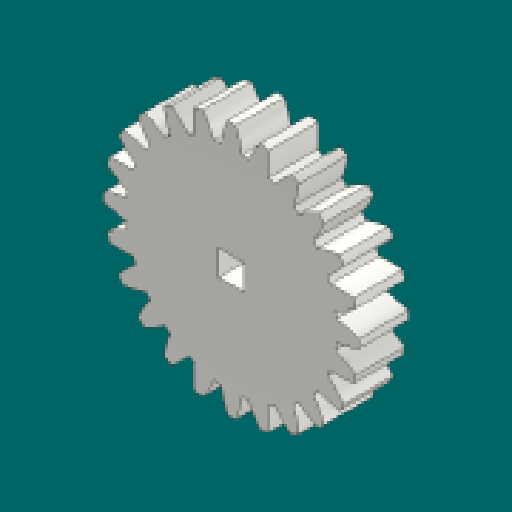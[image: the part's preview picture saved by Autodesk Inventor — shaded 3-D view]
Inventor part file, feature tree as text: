
AUTODESK INVENTOR PART (.ipt)
format: ipt  version: 2023.1 (Build 271208000, 208)  size: 255,488 bytes
history: native  units: mm (DEFAULTED — no unit token found)
features: plane x3, other x3, sketch x3, extrude x2
ambient origin geometry x8: Origin, YZ Plane, XZ Plane, XY Plane, X Axis, Y Axis, Z Axis, Center Point
bodies: Solid1 (feature_tree)
feature tree (11):
  extrude  "Extrusion1"  Depth=6.35mm TaperAngle=0.0deg
  plane  "Work Plane1"
  plane  "Work Plane2"
  plane  "Work Plane3"
  other  "Spur Gear"
  extrude  "Extrusion2"  Depth=76.2mm TaperAngle=0.0deg
  sketch  "Sketch1"  dims[d0=33.02mm d1=6.35mm d2=0.0mm]
  sketch  "Sketch2"  dims[d3=30.48mm d4=76.2mm d5=0.0mm]
  other  "Srf1"
  sketch  "Sketch3"  dims[d6=0.0mm d7=1.308997mm d9=0.0mm d14=0.0mm d15=30.48mm d16=0.0mm d17=0.0mm d18=0.0mm d19=30.48mm d20=3.302mm d21=3.302mm d22=25.4mm d23=0.0mm]
  other  "Pitch Diameter"
